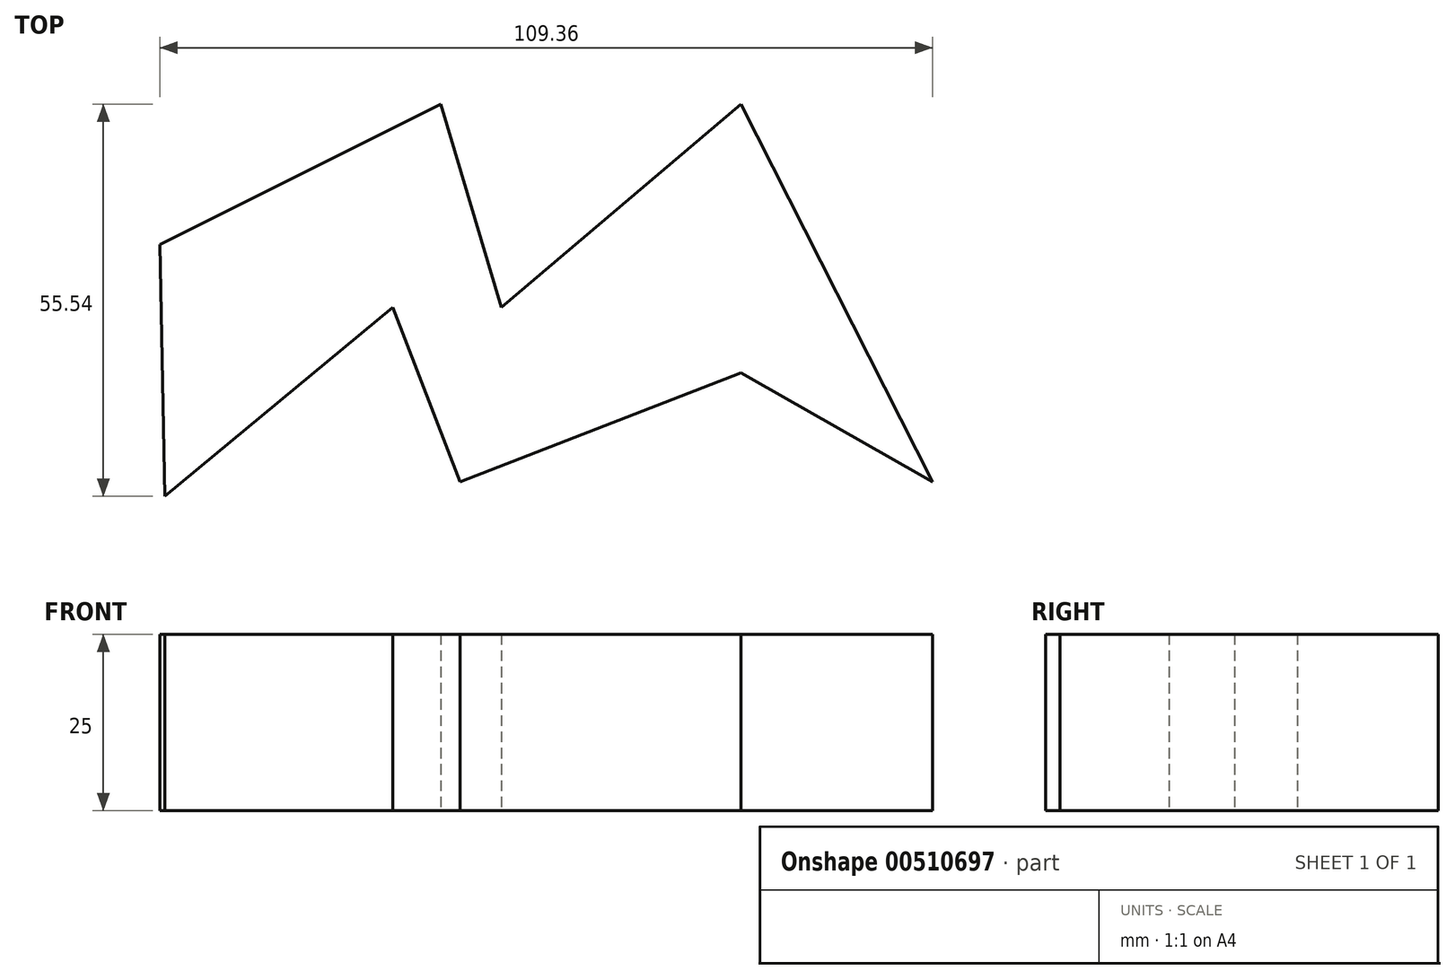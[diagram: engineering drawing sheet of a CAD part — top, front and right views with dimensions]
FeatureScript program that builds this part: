
annotation { "Feature Type Name" : "Feature", "Feature Type Description" : "" }
export const myFeature = defineFeature(function(context is Context, id is Id, definition is map)
    precondition{}
    {
        {
            var Q0;
            Q0=qCreatedBy(makeId("Top.planeOp"),FACE);
            var sketch = newSketch(context, id + "F0", { "sketchPlane" : qUnion([Q0])});
            skLineSegment(sketch, "E0", {"start": v(-57.85, -17.47) * mm, "end": v(-58.54, 18.19) * mm});
            skLineSegment(sketch, "E1", {"start": v(-58.54, 18.19) * mm, "end": v(-18.77, 38.07) * mm});
            skLineSegment(sketch, "E2", {"start": v(-18.77, 38.07) * mm, "end": v(-10.2, 9.27) * mm});
            skLineSegment(sketch, "E3", {"start": v(-10.2, 9.27) * mm, "end": v(23.73, 38.07) * mm});
            skLineSegment(sketch, "E4", {"start": v(23.73, 38.07) * mm, "end": v(50.82, -15.4) * mm});
            skLineSegment(sketch, "E5", {"start": v(50.82, -15.4) * mm, "end": v(23.73, 0) * mm});
            skLineSegment(sketch, "E6", {"start": v(23.73, 0) * mm, "end": v(-16.03, -15.4) * mm});
            skLineSegment(sketch, "E7", {"start": v(-16.03, -15.4) * mm, "end": v(-25.6, 9.27) * mm});
            skLineSegment(sketch, "E8", {"start": v(-25.6, 9.27) * mm, "end": v(-57.85, -17.47) * mm});
            skSolve(sketch);
        }
        {
            var Q0;
            Q0=makeQuery(id+"F0.imprint","IMPRINT",FACE,{"disambiguationData":[TD([[makeQuery(id+"F0.imprint","IMPRINT",EDGE,{"derivedFrom":sQuery(id+"F0.wireOp",EDGE,"E0")}),-1.0]])]});
            extrude(context, id + "F1", {"entities" : qUnion([Q0]), "depth" : 25 * mm});
        }
    });
